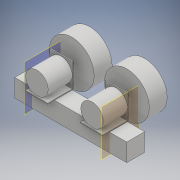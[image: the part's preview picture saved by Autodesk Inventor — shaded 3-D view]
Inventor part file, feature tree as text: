
AUTODESK INVENTOR PART (.ipt)
format: ipt  version: 2018 (Build 220112000, 112)  size: 186,880 bytes
history: native  units: mm
features: extrude x6, sketch x6, plane x2, projected_geometry x1
ambient origin geometry x8: Origin, YZ Plane, XZ Plane, XY Plane, X Axis, Y Axis, Z Axis, Center Point
bodies: Solid1 (feature_tree)
feature tree (15):
  extrude  "Extrusion1"  Depth=40.0mm
  extrude  "Extrusion2"  Depth=50.0mm
  extrude  "Extrusion3"  Depth=50.0mm
  plane  "Work Plane1"
  plane  "Work Plane2"
  extrude  "Extrusion4"  Depth=63.5mm
  extrude  "Extrusion5"  Depth=123.0mm
  extrude  "Extrusion6"  Depth=40.0mm
  sketch  "Sketch1"  dims[d0=250.0mm d1=40.0mm]
  sketch  "Sketch2"  dims[d2=40.0mm d3=0.0mm d4=50.0mm]
  sketch  "Sketch3"  dims[d5=50.0mm d6=28.0mm]
  sketch  "Sketch5"  dims[d7=28.0mm d8=63.5mm]
  sketch  "Sketch6"  dims[d9=63.5mm d10=123.0mm]
  projected_geometry  "Projected Loop1"
  sketch  "Sketch7"  dims[d11=54.0mm d12=0.0mm d13=8.0mm d14=8.0mm d15=23.8mm d16=0.0mm d17=55.0mm d18=2.0mm d19=2.0mm d20=55.0mm d21=50.0mm d22=0.0mm d23=50.0mm d24=0.0mm d25=100.0mm d26=100.0mm d27=40.0mm d28=0.0mm]
